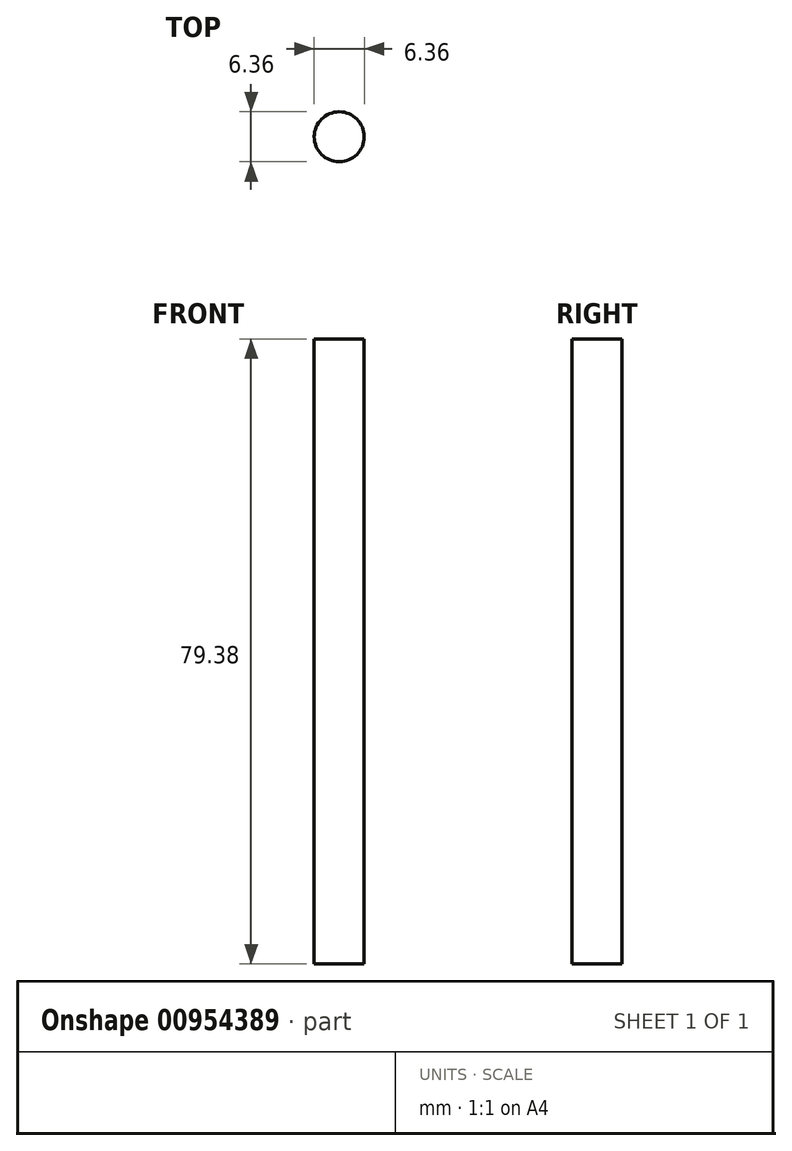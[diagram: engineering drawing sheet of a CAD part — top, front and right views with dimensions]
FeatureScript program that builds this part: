
annotation { "Feature Type Name" : "Feature", "Feature Type Description" : "" }
export const myFeature = defineFeature(function(context is Context, id is Id, definition is map)
    precondition{}
    {
        {
            var Q0;
            Q0=qCreatedBy(makeId("Top.planeOp"),FACE);
            var sketch = newSketch(context, id + "F0", { "sketchPlane" : qUnion([Q0])});
            skCircle(sketch, "E0", {"center": v(0, 0) * mm, "radius": 3.18 * mm});
            skSolve(sketch);
        }
        {
            var Q0;
            Q0 = qSketchRegion(id + "F0", true);
            extrude(context, id + "F1", {"entities" : qUnion([Q0]), "depth" : 79.38 * mm, "offsetDistance" : 25 * mm});
        }
    });
